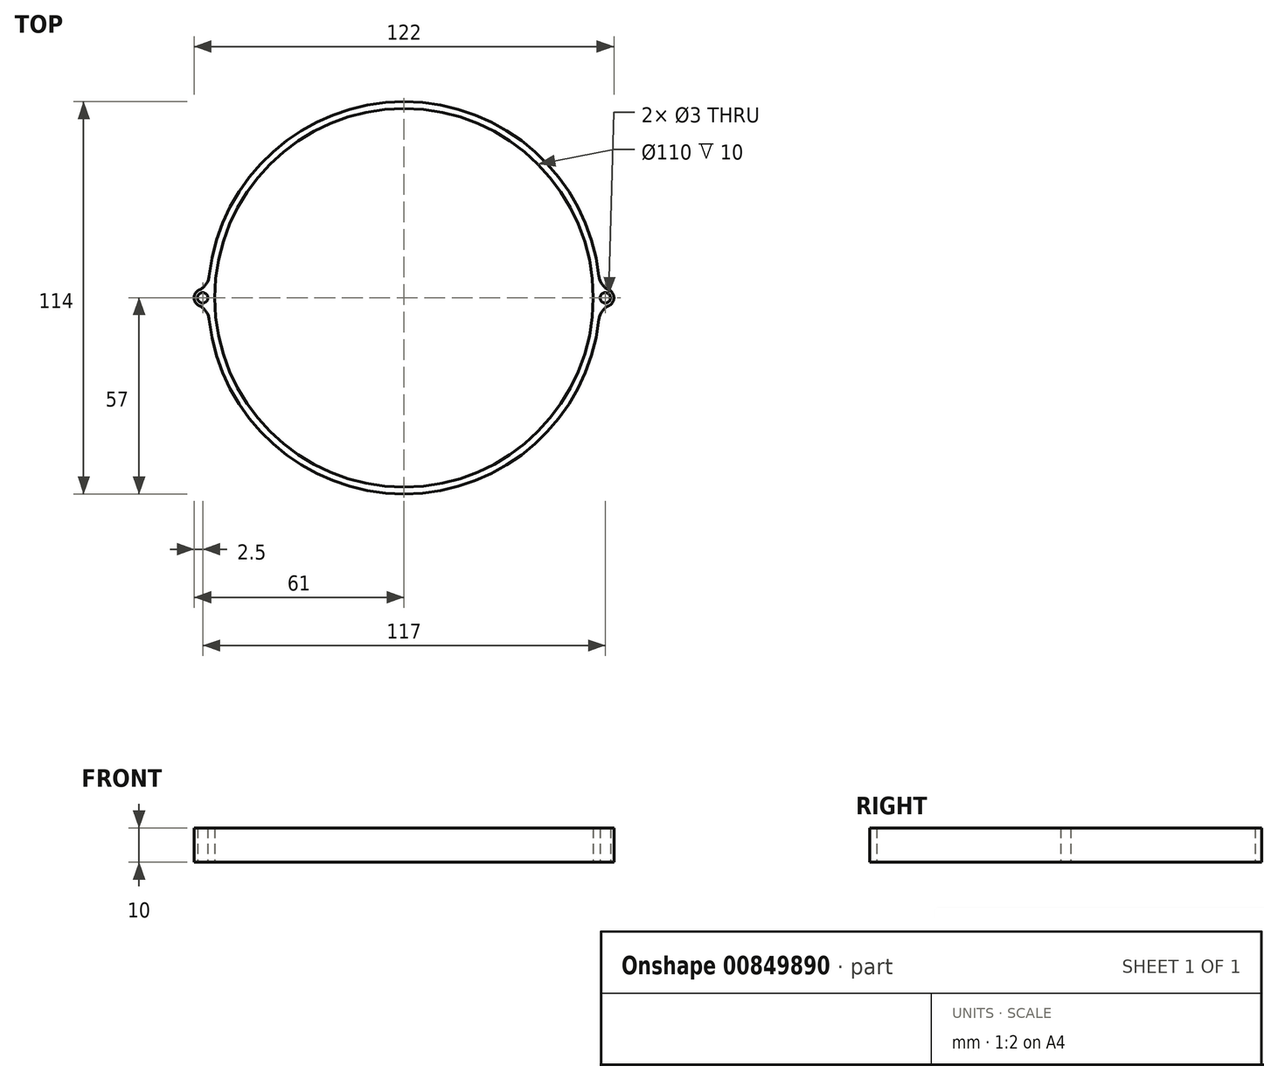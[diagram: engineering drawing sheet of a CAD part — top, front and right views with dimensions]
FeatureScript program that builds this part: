
annotation { "Feature Type Name" : "Feature", "Feature Type Description" : "" }
export const myFeature = defineFeature(function(context is Context, id is Id, definition is map)
    precondition{}
    {
        {
            var Q0;
            Q0=qCreatedBy(makeId("Top.planeOp"),FACE);
            var sketch = newSketch(context, id + "F0", { "sketchPlane" : qUnion([Q0])});
            skCircle(sketch, "E0", {"center": v(0, 0) * mm, "radius": 57 * mm});
            skSolve(sketch);
        }
        {
            var Q0;
            Q0=makeQuery(id+"F0.imprint","IMPRINT",FACE,{"disambiguationData":[TD([[makeQuery(id+"F0.imprint","IMPRINT",EDGE,{"derivedFrom":sQuery(id+"F0.wireOp",EDGE,"E0")}),1.0]])]});
            extrude(context, id + "F1", {"entities" : qUnion([Q0]), "depth" : 10 * mm, "offsetDistance" : 25 * mm});
        }
        {
            var Q0;
            Q0=qCreatedBy(makeId("Top.planeOp"),FACE);
            var sketch = newSketch(context, id + "F2", { "sketchPlane" : qUnion([Q0])});
            skCircle(sketch, "E1", {"center": v(0, 0) * mm, "radius": 55 * mm});
            skSolve(sketch);
        }
        {
            var Q0;
            Q0 = qSketchRegion(id + "F2", true);
            extrude(context, id + "F3", {"entities" : qUnion([Q0]), "operationType" : NewBodyOperationType.REMOVE, "depth" : 25 * mm, "offsetDistance" : 25 * mm});
        }
        {
            var Q0;
            Q0=qCreatedBy(makeId("Top.planeOp"),FACE);
            var sketch = newSketch(context, id + "F4", { "sketchPlane" : qUnion([Q0])});
            skCircle(sketch, "E2", {"center": v(-58.5, 0) * mm, "radius": 1.5 * mm});
            skCircle(sketch, "E3", {"center": v(-58.5, 0) * mm, "radius": 2.5 * mm});
            skCircle(sketch, "E4", {"center": v(58.5, 0) * mm, "radius": 1.5 * mm});
            skCircle(sketch, "E5", {"center": v(58.5, 0) * mm, "radius": 2.5 * mm});
            skSolve(sketch);
        }
        {
            var Q0;
            Q0=makeQuery(id+"F4.imprint","IMPRINT",FACE,{"disambiguationData":[TD([[makeQuery(id+"F4.imprint","IMPRINT",EDGE,{"derivedFrom":sQuery(id+"F4.wireOp",EDGE,"E4")}),-1.0]])]});
            var Q1;
            Q1=makeQuery(id+"F4.imprint","IMPRINT",FACE,{"disambiguationData":[TD([[makeQuery(id+"F4.imprint","IMPRINT",EDGE,{"derivedFrom":sQuery(id+"F4.wireOp",EDGE,"E2")}),-1.0]])]});
            extrude(context, id + "F5", {"entities" : qUnion([Q0, Q1]), "operationType" : NewBodyOperationType.ADD, "depth" : 10 * mm, "offsetDistance" : 25 * mm});
        }
        {
            var Q0;
            Q0=makeQuery(id+"F5.boolean.opBoolean","INTERSECT",EDGE,{"disambiguationData":[OD(0.0)],"derivedFrom":[makeQuery(id+"F1.opExtrude","SWEPT_FACE",FACE,{"disambiguationData":[OSD([sQuery(id+"F0.wireOp",EDGE,"E0")])]}),makeQuery(id+"F5.opExtrude","SWEPT_FACE",FACE,{"disambiguationData":[OSD([sQuery(id+"F4.wireOp",EDGE,"E3")])]})]});
            var Q1;
            Q1=makeQuery(id+"F5.boolean.opBoolean","INTERSECT",EDGE,{"disambiguationData":[OD(1.0)],"derivedFrom":[makeQuery(id+"F1.opExtrude","SWEPT_FACE",FACE,{"disambiguationData":[OSD([sQuery(id+"F0.wireOp",EDGE,"E0")])]}),makeQuery(id+"F5.opExtrude","SWEPT_FACE",FACE,{"disambiguationData":[OSD([sQuery(id+"F4.wireOp",EDGE,"E3")])]})]});
            fillet(context, id + "F6", {"entities" : qUnion([Q0, Q1]), "radius" : 5 * mm, "tangentPropagation" : true, "allowEdgeOverflow" : false});
        }
        {
            var Q0;
            Q0=makeQuery(id+"F5.boolean.opBoolean","INTERSECT",EDGE,{"disambiguationData":[OD(0.0)],"derivedFrom":[makeQuery(id+"F1.opExtrude","SWEPT_FACE",FACE,{"disambiguationData":[OSD([sQuery(id+"F0.wireOp",EDGE,"E0")])]}),makeQuery(id+"F5.opExtrude","SWEPT_FACE",FACE,{"disambiguationData":[OSD([sQuery(id+"F4.wireOp",EDGE,"E5")])]})]});
            var Q1;
            Q1=makeQuery(id+"F5.boolean.opBoolean","INTERSECT",EDGE,{"disambiguationData":[OD(1.0)],"derivedFrom":[makeQuery(id+"F1.opExtrude","SWEPT_FACE",FACE,{"disambiguationData":[OSD([sQuery(id+"F0.wireOp",EDGE,"E0")])]}),makeQuery(id+"F5.opExtrude","SWEPT_FACE",FACE,{"disambiguationData":[OSD([sQuery(id+"F4.wireOp",EDGE,"E5")])]})]});
            fillet(context, id + "F7", {"entities" : qUnion([Q0, Q1]), "radius" : 5 * mm, "tangentPropagation" : true, "allowEdgeOverflow" : false});
        }
    });
